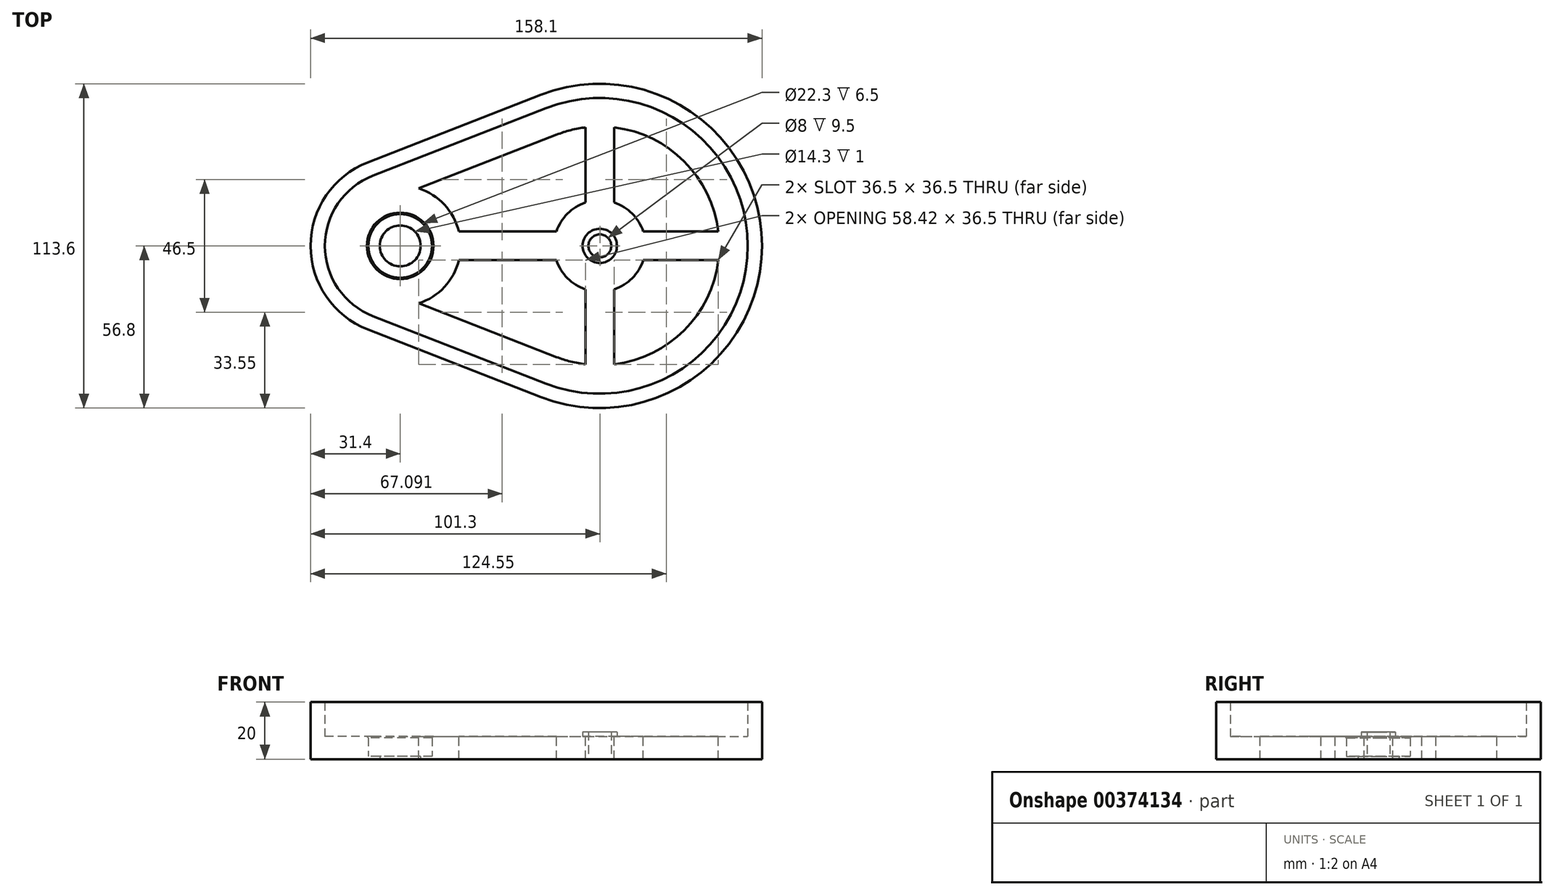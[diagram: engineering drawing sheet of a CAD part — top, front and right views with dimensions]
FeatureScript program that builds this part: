
annotation { "Feature Type Name" : "Feature", "Feature Type Description" : "" }
export const myFeature = defineFeature(function(context is Context, id is Id, definition is map)
    precondition{}
    {
        {
            var Q0;
            Q0=qCreatedBy(makeId("Top.planeOp"),FACE);
            var sketch = newSketch(context, id + "F0", { "sketchPlane" : qUnion([Q0])});
            skLineSegment(sketch, "E0", {"start": v(-34.95, 0) * mm, "end": v(34.95, 0) * mm, "construction": true});
            skPoint(sketch, "E1", {"position": v(0, 0) * mm});
            skCircle(sketch, "E2", {"center": v(-34.95, 0) * mm, "radius": 11.15 * mm});
            skCircle(sketch, "E3", {"center": v(34.95, 0) * mm, "radius": 4 * mm});
            skLineSegment(sketch, "E4", {"start": v(16.13, 48.26) * mm, "end": v(-44.54, 24.6) * mm});
            skLineSegment(sketch, "E5", {"start": v(-44.54, -24.6) * mm, "end": v(16.13, -48.26) * mm});
            skArc(sketch, "E6.trimOffspring", {"start": v(16.13, -48.26) * mm, "mid": v(86.75, 0) * mm, "end": v(16.13, 48.26) * mm});
            skArc(sketch, "E7.trimOffspring", {"start": v(-44.54, 24.6) * mm, "mid": v(-61.35, 0) * mm, "end": v(-44.54, -24.6) * mm});
            skLineSegment(sketch, "E8.0", {"start": v(14.31, 52.92) * mm, "end": v(-46.36, 29.25) * mm});
            skArc(sketch, "E8.1", {"start": v(14.31, -52.92) * mm, "mid": v(91.75, 0) * mm, "end": v(14.31, 52.92) * mm});
            skLineSegment(sketch, "E8.2", {"start": v(-46.36, -29.25) * mm, "end": v(14.31, -52.92) * mm});
            skArc(sketch, "E8.3", {"start": v(-46.36, 29.25) * mm, "mid": v(-66.35, 0) * mm, "end": v(-46.36, -29.25) * mm});
            skCircle(sketch, "E9.0", {"center": v(-34.95, 0) * mm, "radius": 7.15 * mm});
            skSolve(sketch);
        }
        {
            var Q0;
            Q0 = qSketchRegion(id + "F0", true);
            var Q1;
            Q1=makeQuery(id+"F0.imprint","IMPRINT",FACE,{"disambiguationData":[TD([[makeQuery(id+"F0.imprint","IMPRINT",EDGE,{"derivedFrom":sQuery(id+"F0.wireOp",EDGE,"E2")}),-1.0]])]});
            extrude(context, id + "F1", {"entities" : qUnion([Q0, Q1]), "depth" : 8 * mm});
        }
        {
            var Q0;
            Q0=makeQuery(id+"F0.imprint","IMPRINT",FACE,{"disambiguationData":[TD([[makeQuery(id+"F0.imprint","IMPRINT",EDGE,{"derivedFrom":sQuery(id+"F0.wireOp",EDGE,"E2")}),1.0]])]});
            extrude(context, id + "F2", {"entities" : qUnion([Q0]), "operationType" : NewBodyOperationType.ADD, "depth" : 1 * mm});
        }
        {
            var Q0;
            Q0=makeQuery(id+"F1.opExtrude","CAP_EDGE",EDGE,{"disambiguationData":[OSD([sQuery(id+"F0.wireOp",EDGE,"E2")])],"isStart":false});
            chamfer(context, id + "F3", {"entities" : qUnion([Q0]), "width" : 0.5 * mm, "tangentPropagation" : true});
        }
        {
            var Q0;
            Q0=makeQuery(id+"F1.opExtrude","CAP_FACE",FACE,{"disambiguationData":[OSD([sQuery(id+"F0.wireOp",EDGE,"E2"),sQuery(id+"F0.wireOp",EDGE,"E3"),sQuery(id+"F0.wireOp",EDGE,"E8.0"),sQuery(id+"F0.wireOp",EDGE,"E8.1"),sQuery(id+"F0.wireOp",EDGE,"E8.2"),sQuery(id+"F0.wireOp",EDGE,"E8.3")])],"isStart":false});
            var sketch = newSketch(context, id + "F4", { "sketchPlane" : qUnion([Q0])});
            skCircle(sketch, "E10.0", {"center": v(34.95, 0) * mm, "radius": 4 * mm});
            skCircle(sketch, "E11.0", {"center": v(34.95, 0) * mm, "radius": 6 * mm});
            skSolve(sketch);
        }
        {
            var Q0;
            Q0 = qSketchRegion(id + "F4", true);
            extrude(context, id + "F5", {"entities" : qUnion([Q0]), "operationType" : NewBodyOperationType.ADD, "depth" : 1.5 * mm});
        }
        {
            var Q0;
            Q0=makeQuery(id+"F0.imprint","IMPRINT",FACE,{"disambiguationData":[TD([[makeQuery(id+"F0.imprint","IMPRINT",EDGE,{"derivedFrom":sQuery(id+"F0.wireOp",EDGE,"E4")}),-1.0]])]});
            extrude(context, id + "F6", {"entities" : qUnion([Q0]), "operationType" : NewBodyOperationType.ADD, "depth" : 20 * mm});
        }
        {
            var Q0;
            Q0=makeQuery(id+"F1.opExtrude","CAP_FACE",FACE,{"disambiguationData":[OSD([sQuery(id+"F0.wireOp",EDGE,"E2"),sQuery(id+"F0.wireOp",EDGE,"E3"),sQuery(id+"F0.wireOp",EDGE,"E8.0"),sQuery(id+"F0.wireOp",EDGE,"E8.1"),sQuery(id+"F0.wireOp",EDGE,"E8.2"),sQuery(id+"F0.wireOp",EDGE,"E8.3")])],"isStart":false});
            var sketch = newSketch(context, id + "F7", { "sketchPlane" : qUnion([Q0])});
            skLineSegment(sketch, "E12.0", {"start": v(16.13, 48.26) * mm, "end": v(-44.54, 24.6) * mm});
            skLineSegment(sketch, "E13.0", {"start": v(-44.54, -24.6) * mm, "end": v(16.13, -48.26) * mm});
            skLineSegment(sketch, "E14.0", {"start": v(19.76, 38.94) * mm, "end": v(-28.47, 20.13) * mm});
            skCircle(sketch, "E15.0", {"center": v(-34.95, 0) * mm, "radius": 11.15 * mm});
            skArc(sketch, "E16.0", {"start": v(-28.47, -20.13) * mm, "mid": v(-13.8, 0) * mm, "end": v(-28.47, 20.13) * mm});
            skLineSegment(sketch, "E17.0", {"start": v(-28.47, -20.13) * mm, "end": v(19.76, -38.94) * mm});
            skCircle(sketch, "E18.0", {"center": v(34.95, 0) * mm, "radius": 6 * mm});
            skCircle(sketch, "E19.0", {"center": v(34.95, 0) * mm, "radius": 16 * mm});
            skArc(sketch, "E20.0", {"start": v(16.13, -48.26) * mm, "mid": v(86.75, 0) * mm, "end": v(16.13, 48.26) * mm});
            skArc(sketch, "E21.0", {"start": v(19.76, -38.94) * mm, "mid": v(76.75, 0) * mm, "end": v(19.76, 38.94) * mm});
            skLineSegment(sketch, "E22.trimOffspring", {"start": v(29.95, 15.2) * mm, "end": v(29.95, 41.5) * mm});
            skLineSegment(sketch, "E23.trimOffspring", {"start": v(39.95, 15.2) * mm, "end": v(39.95, 41.5) * mm});
            skLineSegment(sketch, "E24.1.0", {"start": v(50.15, -5) * mm, "end": v(76.45, -5) * mm});
            skLineSegment(sketch, "E24.1.1", {"start": v(50.15, 5) * mm, "end": v(76.45, 5) * mm});
            skLineSegment(sketch, "E24.2.0", {"start": v(29.95, -15.2) * mm, "end": v(29.95, -41.5) * mm});
            skLineSegment(sketch, "E24.2.1", {"start": v(39.95, -15.2) * mm, "end": v(39.95, -41.5) * mm});
            skLineSegment(sketch, "E25", {"start": v(19.75, 5) * mm, "end": v(-14.4, 5) * mm});
            skLineSegment(sketch, "E26", {"start": v(19.75, -5) * mm, "end": v(-14.4, -5) * mm});
            skSolve(sketch);
        }
        {
            var Q0;
            {var subQ1=sQuery(id+"F7.wireOp",EDGE,"E14.0");Q0=makeQuery(id+"F7.imprint","IMPRINT",FACE,{"disambiguationData":[TD([[makeQuery(id+"F7.imprint","IMPRINT",EDGE,{"derivedFrom":subQ1}),1.0]])]});}
            var Q1;
            {var subQ0=sQuery(id+"F7.wireOp",EDGE,"E23.trimOffspring");Q1=makeQuery(id+"F7.imprint","IMPRINT",FACE,{"disambiguationData":[TD([[makeQuery(id+"F7.imprint","IMPRINT",EDGE,{"derivedFrom":subQ0}),-1.0]])]});}
            var Q2;
            {var subQ1=sQuery(id+"F7.wireOp",EDGE,"E17.0");Q2=makeQuery(id+"F7.imprint","IMPRINT",FACE,{"disambiguationData":[TD([[makeQuery(id+"F7.imprint","IMPRINT",EDGE,{"derivedFrom":subQ1}),1.0]])]});}
            var Q3;
            {var subQ0=sQuery(id+"F7.wireOp",EDGE,"E24.1.0");Q3=makeQuery(id+"F7.imprint","IMPRINT",FACE,{"disambiguationData":[TD([[makeQuery(id+"F7.imprint","IMPRINT",EDGE,{"derivedFrom":subQ0}),-1.0]])]});}
            extrude(context, id + "F8", {"entities" : qUnion([Q0, Q1, Q2, Q3]), "operationType" : NewBodyOperationType.REMOVE, "oppositeDirection" : true, "depth" : 25 * mm});
        }
    });
